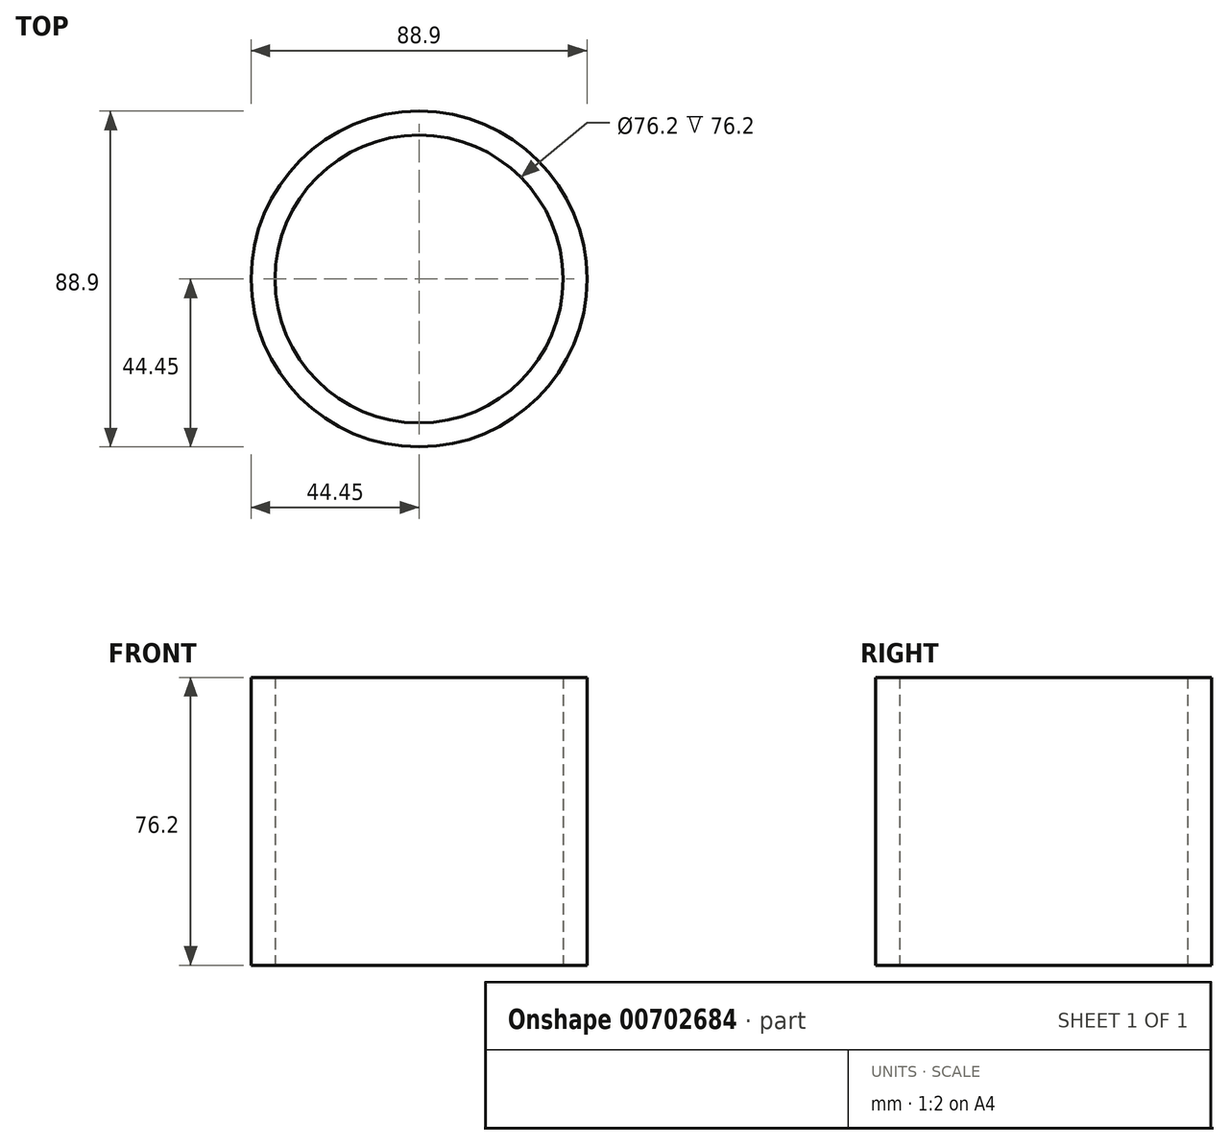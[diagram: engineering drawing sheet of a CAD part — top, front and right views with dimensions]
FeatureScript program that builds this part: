
annotation { "Feature Type Name" : "Feature", "Feature Type Description" : "" }
export const myFeature = defineFeature(function(context is Context, id is Id, definition is map)
    precondition{}
    {
        {
            var Q0;
            Q0=qCreatedBy(makeId("Top.planeOp"),FACE);
            var sketch = newSketch(context, id + "F0", { "sketchPlane" : qUnion([Q0])});
            skCircle(sketch, "E0", {"center": v(0, 0) * mm, "radius": 44.45 * mm});
            skCircle(sketch, "E1", {"center": v(0, 0) * mm, "radius": 38.1 * mm});
            skSolve(sketch);
        }
        {
            var Q0;
            Q0 = qSketchRegion(id + "F0", true);
            extrude(context, id + "F1", {"entities" : qUnion([Q0]), "depth" : 76.2 * mm, "offsetDistance" : 25.4 * mm});
        }
    });
